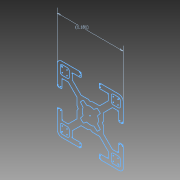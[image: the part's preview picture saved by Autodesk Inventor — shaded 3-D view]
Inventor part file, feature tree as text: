
AUTODESK INVENTOR PART (.ipt)
format: ipt  version: 2011 (Build 150239000, 239)  size: 111,616 bytes
history: native  units: in
note: dims shown in document units (in); Inventor stores cm internally (conversion verified against a paired STEP export)
features: sketch x1
ambient origin geometry x8: Origin, YZ Plane, XZ Plane, XY Plane, X Axis, Y Axis, Z Axis, Center Point
feature tree (1):
  sketch  "Sketch1"  dims[d1=1.1811in]
